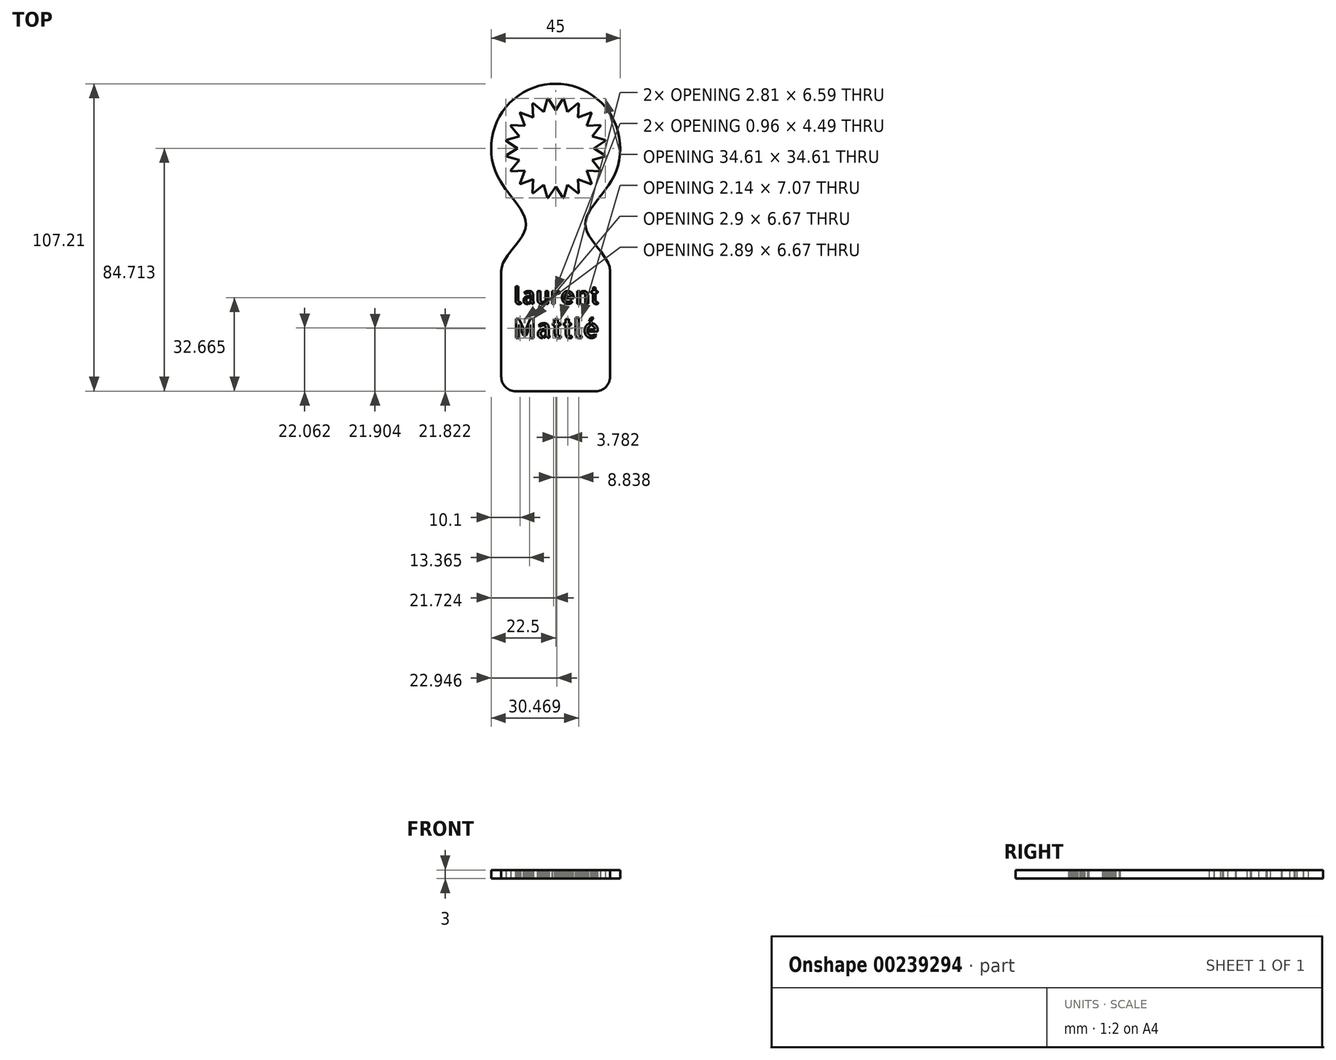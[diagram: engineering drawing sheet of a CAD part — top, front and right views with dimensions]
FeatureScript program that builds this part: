
annotation { "Feature Type Name" : "Feature", "Feature Type Description" : "" }
export const myFeature = defineFeature(function(context is Context, id is Id, definition is map)
    precondition{}
    {
        {
            var Q0;
            Q0=qCreatedBy(makeId("Top.planeOp"),FACE);
            var sketch = newSketch(context, id + "F0", { "sketchPlane" : qUnion([Q0])});
            skCircle(sketch, "E0", {"center": v(0, 8.25) * mm, "radius": 22.5 * mm});
            skLineSegment(sketch, "E1.bottom", {"start": v(-18.96, -34.53) * mm, "end": v(18.96, -34.53) * mm});
            skLineSegment(sketch, "E1.top", {"start": v(-13.96, -76.46) * mm, "end": v(13.96, -76.46) * mm});
            skLineSegment(sketch, "E1.left", {"start": v(-18.96, -34.53) * mm, "end": v(-18.96, -71.46) * mm});
            skLineSegment(sketch, "E1.right", {"start": v(18.96, -34.53) * mm, "end": v(18.96, -71.46) * mm});
            skFitSpline(sketch, "E2", {"points": [v(-19.33, -3.26) * mm, v(-10.41, -19.12) * mm, v(-18.96, -34.53) * mm], "startDerivative": vector(18.85, -32.07) * mm, "endDerivative": vector(0, -31.43) * mm});
            skFitSpline(sketch, "E3.MirrorCS", {"points": [v(19.33, -3.26) * mm, v(10.41, -19.12) * mm, v(18.96, -34.53) * mm], "startDerivative": vector(-18.85, -32.07) * mm, "endDerivative": vector(0, -31.43) * mm});
            skPoint(sketch, "E4.visualSharp", {"position": v(-18.96, -76.46) * mm});
            skArc(sketch, "E4.filletArc", {"start": v(-18.96, -71.46) * mm, "mid": v(-17.5, -75) * mm, "end": v(-13.96, -76.46) * mm});
            skPoint(sketch, "E5.visualSharp", {"position": v(18.96, -76.46) * mm});
            skArc(sketch, "E5.filletArc", {"start": v(13.96, -76.46) * mm, "mid": v(17.5, -75) * mm, "end": v(18.96, -71.46) * mm});
            skCircle(sketch, "E6", {"center": v(0, 8.25) * mm, "radius": 17.5 * mm});
            skLineSegment(sketch, "E7", {"start": v(-2.6, 25.56) * mm, "end": v(0, 21.59) * mm});
            skLineSegment(sketch, "E8", {"start": v(0, 21.59) * mm, "end": v(2.6, 25.56) * mm});
            skLineSegment(sketch, "E9.1.0", {"start": v(-7.82, 23.9) * mm, "end": v(-4.12, 20.93) * mm});
            skLineSegment(sketch, "E9.1.1", {"start": v(-4.12, 20.93) * mm, "end": v(-2.88, 25.51) * mm});
            skLineSegment(sketch, "E9.2.0", {"start": v(-12.27, 20.73) * mm, "end": v(-7.84, 19.04) * mm});
            skLineSegment(sketch, "E9.2.1", {"start": v(-7.84, 19.04) * mm, "end": v(-8.07, 23.78) * mm});
            skLineSegment(sketch, "E10.2.3.0", {"start": v(-15.53, 16.32) * mm, "end": v(-10.79, 16.1) * mm});
            skLineSegment(sketch, "E10.3.3.0", {"start": v(-10.79, 16.1) * mm, "end": v(-12.47, 20.53) * mm});
            skLineSegment(sketch, "E10.2.4.0", {"start": v(-17.26, 11.13) * mm, "end": v(-12.68, 12.37) * mm});
            skLineSegment(sketch, "E10.3.4.0", {"start": v(-12.68, 12.37) * mm, "end": v(-15.66, 16.07) * mm});
            skLineSegment(sketch, "E10.2.5.0", {"start": v(-17.3, 5.66) * mm, "end": v(-13.33, 8.25) * mm});
            skLineSegment(sketch, "E10.3.5.0", {"start": v(-13.33, 8.25) * mm, "end": v(-17.3, 10.85) * mm});
            skLineSegment(sketch, "E10.2.6.0", {"start": v(-15.66, 0.44) * mm, "end": v(-12.68, 4.13) * mm});
            skLineSegment(sketch, "E10.3.6.0", {"start": v(-12.68, 4.13) * mm, "end": v(-17.26, 5.38) * mm});
            skLineSegment(sketch, "E10.2.7.0", {"start": v(-12.47, -4.02) * mm, "end": v(-10.79, 0.42) * mm});
            skLineSegment(sketch, "E10.3.7.0", {"start": v(-10.79, 0.42) * mm, "end": v(-15.53, 0.18) * mm});
            skLineSegment(sketch, "E10.2.8.0", {"start": v(-8.07, -7.27) * mm, "end": v(-7.84, -2.53) * mm});
            skLineSegment(sketch, "E10.3.8.0", {"start": v(-7.84, -2.53) * mm, "end": v(-12.27, -4.22) * mm});
            skLineSegment(sketch, "E10.2.9.0", {"start": v(-2.88, -9) * mm, "end": v(-4.12, -4.43) * mm});
            skLineSegment(sketch, "E10.3.9.0", {"start": v(-4.12, -4.43) * mm, "end": v(-7.82, -7.4) * mm});
            skLineSegment(sketch, "E10.2.10.0", {"start": v(2.6, -9.05) * mm, "end": v(0, -5.08) * mm});
            skLineSegment(sketch, "E10.3.10.0", {"start": v(0, -5.08) * mm, "end": v(-2.6, -9.05) * mm});
            skLineSegment(sketch, "E10.2.11.0", {"start": v(7.82, -7.4) * mm, "end": v(4.12, -4.43) * mm});
            skLineSegment(sketch, "E10.3.11.0", {"start": v(4.12, -4.43) * mm, "end": v(2.88, -9) * mm});
            skLineSegment(sketch, "E10.2.12.0", {"start": v(12.27, -4.22) * mm, "end": v(7.84, -2.53) * mm});
            skLineSegment(sketch, "E10.3.12.0", {"start": v(7.84, -2.53) * mm, "end": v(8.07, -7.27) * mm});
            skLineSegment(sketch, "E10.2.13.0", {"start": v(15.53, 0.18) * mm, "end": v(10.79, 0.42) * mm});
            skLineSegment(sketch, "E10.3.13.0", {"start": v(10.79, 0.42) * mm, "end": v(12.47, -4.02) * mm});
            skLineSegment(sketch, "E10.2.14.0", {"start": v(17.26, 5.38) * mm, "end": v(12.68, 4.13) * mm});
            skLineSegment(sketch, "E10.3.14.0", {"start": v(12.68, 4.13) * mm, "end": v(15.66, 0.44) * mm});
            skLineSegment(sketch, "E10.2.15.0", {"start": v(17.3, 10.85) * mm, "end": v(13.33, 8.25) * mm});
            skLineSegment(sketch, "E10.3.15.0", {"start": v(13.33, 8.25) * mm, "end": v(17.3, 5.66) * mm});
            skLineSegment(sketch, "E10.2.16.0", {"start": v(15.66, 16.07) * mm, "end": v(12.68, 12.37) * mm});
            skLineSegment(sketch, "E10.3.16.0", {"start": v(12.68, 12.37) * mm, "end": v(17.26, 11.13) * mm});
            skLineSegment(sketch, "E10.2.17.0", {"start": v(12.47, 20.53) * mm, "end": v(10.79, 16.1) * mm});
            skLineSegment(sketch, "E10.3.17.0", {"start": v(10.79, 16.1) * mm, "end": v(15.53, 16.32) * mm});
            skLineSegment(sketch, "E10.2.18.0", {"start": v(8.07, 23.78) * mm, "end": v(7.84, 19.04) * mm});
            skLineSegment(sketch, "E10.3.18.0", {"start": v(7.84, 19.04) * mm, "end": v(12.27, 20.73) * mm});
            skLineSegment(sketch, "E10.2.19.0", {"start": v(2.88, 25.51) * mm, "end": v(4.12, 20.93) * mm});
            skLineSegment(sketch, "E10.3.19.0", {"start": v(4.12, 20.93) * mm, "end": v(7.82, 23.9) * mm});
            skSolve(sketch);
        }
        {
            var Q0;
            {var subQ27=sQuery(id+"F0.wireOp",EDGE,"E0");var subQ28=makeQuery(id+"F0.imprint","INTERSECT",VERTEX,{"derivedFrom":[subQ27,sQuery(id+"F0.wireOp",EDGE,"E2")]});Q0=makeQuery(id+"F0.imprint","IMPRINT",FACE,{"disambiguationData":[TD([[makeQuery(id+"F0.imprint","IMPRINT",EDGE,{"disambiguationData":[TD([[subQ28,-1.0]])],"derivedFrom":subQ27}),1.0]])]});}
            var Q1;
            {var subQ0=sQuery(id+"F0.wireOp",EDGE,"E10.2.4.0");Q1=makeQuery(id+"F0.imprint","IMPRINT",FACE,{"disambiguationData":[TD([[makeQuery(id+"F0.imprint","IMPRINT",EDGE,{"derivedFrom":subQ0}),1.0]])]});}
            var Q2;
            {var subQ0=sQuery(id+"F0.wireOp",EDGE,"E10.2.3.0");Q2=makeQuery(id+"F0.imprint","IMPRINT",FACE,{"disambiguationData":[TD([[makeQuery(id+"F0.imprint","IMPRINT",EDGE,{"derivedFrom":subQ0}),1.0]])]});}
            var Q3;
            {var subQ0=sQuery(id+"F0.wireOp",EDGE,"E10.2.5.0");Q3=makeQuery(id+"F0.imprint","IMPRINT",FACE,{"disambiguationData":[TD([[makeQuery(id+"F0.imprint","IMPRINT",EDGE,{"derivedFrom":subQ0}),1.0]])]});}
            var Q4;
            {var subQ0=sQuery(id+"F0.wireOp",EDGE,"E10.2.6.0");Q4=makeQuery(id+"F0.imprint","IMPRINT",FACE,{"disambiguationData":[TD([[makeQuery(id+"F0.imprint","IMPRINT",EDGE,{"derivedFrom":subQ0}),1.0]])]});}
            var Q5;
            {var subQ0=sQuery(id+"F0.wireOp",EDGE,"E10.2.7.0");Q5=makeQuery(id+"F0.imprint","IMPRINT",FACE,{"disambiguationData":[TD([[makeQuery(id+"F0.imprint","IMPRINT",EDGE,{"derivedFrom":subQ0}),1.0]])]});}
            var Q6;
            {var subQ0=sQuery(id+"F0.wireOp",EDGE,"E10.2.8.0");Q6=makeQuery(id+"F0.imprint","IMPRINT",FACE,{"disambiguationData":[TD([[makeQuery(id+"F0.imprint","IMPRINT",EDGE,{"derivedFrom":subQ0}),1.0]])]});}
            var Q7;
            {var subQ0=sQuery(id+"F0.wireOp",EDGE,"E10.2.9.0");Q7=makeQuery(id+"F0.imprint","IMPRINT",FACE,{"disambiguationData":[TD([[makeQuery(id+"F0.imprint","IMPRINT",EDGE,{"derivedFrom":subQ0}),1.0]])]});}
            var Q8;
            {var subQ0=sQuery(id+"F0.wireOp",EDGE,"E10.2.10.0");Q8=makeQuery(id+"F0.imprint","IMPRINT",FACE,{"disambiguationData":[TD([[makeQuery(id+"F0.imprint","IMPRINT",EDGE,{"derivedFrom":subQ0}),1.0]])]});}
            var Q9;
            {var subQ0=sQuery(id+"F0.wireOp",EDGE,"E10.2.11.0");Q9=makeQuery(id+"F0.imprint","IMPRINT",FACE,{"disambiguationData":[TD([[makeQuery(id+"F0.imprint","IMPRINT",EDGE,{"derivedFrom":subQ0}),1.0]])]});}
            var Q10;
            {var subQ0=sQuery(id+"F0.wireOp",EDGE,"E10.2.12.0");Q10=makeQuery(id+"F0.imprint","IMPRINT",FACE,{"disambiguationData":[TD([[makeQuery(id+"F0.imprint","IMPRINT",EDGE,{"derivedFrom":subQ0}),1.0]])]});}
            var Q11;
            {var subQ0=sQuery(id+"F0.wireOp",EDGE,"E10.2.13.0");Q11=makeQuery(id+"F0.imprint","IMPRINT",FACE,{"disambiguationData":[TD([[makeQuery(id+"F0.imprint","IMPRINT",EDGE,{"derivedFrom":subQ0}),1.0]])]});}
            var Q12;
            {var subQ0=sQuery(id+"F0.wireOp",EDGE,"E10.2.14.0");Q12=makeQuery(id+"F0.imprint","IMPRINT",FACE,{"disambiguationData":[TD([[makeQuery(id+"F0.imprint","IMPRINT",EDGE,{"derivedFrom":subQ0}),1.0]])]});}
            var Q13;
            {var subQ0=sQuery(id+"F0.wireOp",EDGE,"E10.2.15.0");Q13=makeQuery(id+"F0.imprint","IMPRINT",FACE,{"disambiguationData":[TD([[makeQuery(id+"F0.imprint","IMPRINT",EDGE,{"derivedFrom":subQ0}),1.0]])]});}
            var Q14;
            {var subQ0=sQuery(id+"F0.wireOp",EDGE,"E10.2.16.0");Q14=makeQuery(id+"F0.imprint","IMPRINT",FACE,{"disambiguationData":[TD([[makeQuery(id+"F0.imprint","IMPRINT",EDGE,{"derivedFrom":subQ0}),1.0]])]});}
            var Q15;
            {var subQ0=sQuery(id+"F0.wireOp",EDGE,"E10.2.17.0");Q15=makeQuery(id+"F0.imprint","IMPRINT",FACE,{"disambiguationData":[TD([[makeQuery(id+"F0.imprint","IMPRINT",EDGE,{"derivedFrom":subQ0}),1.0]])]});}
            var Q16;
            {var subQ0=sQuery(id+"F0.wireOp",EDGE,"E10.2.18.0");Q16=makeQuery(id+"F0.imprint","IMPRINT",FACE,{"disambiguationData":[TD([[makeQuery(id+"F0.imprint","IMPRINT",EDGE,{"derivedFrom":subQ0}),1.0]])]});}
            var Q17;
            {var subQ0=sQuery(id+"F0.wireOp",EDGE,"E10.2.19.0");Q17=makeQuery(id+"F0.imprint","IMPRINT",FACE,{"disambiguationData":[TD([[makeQuery(id+"F0.imprint","IMPRINT",EDGE,{"derivedFrom":subQ0}),1.0]])]});}
            var Q18;
            {var subQ0=sQuery(id+"F0.wireOp",EDGE,"E7");Q18=makeQuery(id+"F0.imprint","IMPRINT",FACE,{"disambiguationData":[TD([[makeQuery(id+"F0.imprint","IMPRINT",EDGE,{"derivedFrom":subQ0}),1.0]])]});}
            var Q19;
            {var subQ0=sQuery(id+"F0.wireOp",EDGE,"E9.1.0");Q19=makeQuery(id+"F0.imprint","IMPRINT",FACE,{"disambiguationData":[TD([[makeQuery(id+"F0.imprint","IMPRINT",EDGE,{"derivedFrom":subQ0}),1.0]])]});}
            var Q20;
            {var subQ0=sQuery(id+"F0.wireOp",EDGE,"E9.2.0");Q20=makeQuery(id+"F0.imprint","IMPRINT",FACE,{"disambiguationData":[TD([[makeQuery(id+"F0.imprint","IMPRINT",EDGE,{"derivedFrom":subQ0}),1.0]])]});}
            var Q21;
            Q21=makeQuery(id+"F0.imprint","IMPRINT",FACE,{"disambiguationData":[TD([[makeQuery(id+"F0.imprint","IMPRINT",EDGE,{"derivedFrom":sQuery(id+"F0.wireOp",EDGE,"E1.bottom")}),1.0]])]});
            var Q22;
            Q22=makeQuery(id+"F0.imprint","IMPRINT",FACE,{"disambiguationData":[TD([[makeQuery(id+"F0.imprint","IMPRINT",EDGE,{"derivedFrom":sQuery(id+"F0.wireOp",EDGE,"E1.bottom")}),-1.0]])]});
            extrude(context, id + "F1", {"entities" : qUnion([Q0, Q1, Q2, Q3, Q4, Q5, Q6, Q7, Q8, Q9, Q10, Q11, Q12, Q13, Q14, Q15, Q16, Q17, Q18, Q19, Q20, Q21, Q22]), "depth" : 3 * mm});
        }
        {
            var Q0;
            Q0=makeQuery(id+"F1.opExtrude","CAP_FACE",FACE,{"disambiguationData":[OSD([sQuery(id+"F0.wireOp",EDGE,"E0"),sQuery(id+"F0.wireOp",EDGE,"E1.top"),sQuery(id+"F0.wireOp",EDGE,"E1.left"),sQuery(id+"F0.wireOp",EDGE,"E1.right"),sQuery(id+"F0.wireOp",EDGE,"E2"),sQuery(id+"F0.wireOp",EDGE,"E3.MirrorCS"),sQuery(id+"F0.wireOp",EDGE,"E4.filletArc"),sQuery(id+"F0.wireOp",EDGE,"E5.filletArc"),sQuery(id+"F0.wireOp",EDGE,"E6"),sQuery(id+"F0.wireOp",EDGE,"E7"),sQuery(id+"F0.wireOp",EDGE,"E8"),sQuery(id+"F0.wireOp",EDGE,"E9.1.0"),sQuery(id+"F0.wireOp",EDGE,"E9.1.1"),sQuery(id+"F0.wireOp",EDGE,"E9.2.0"),sQuery(id+"F0.wireOp",EDGE,"E9.2.1"),sQuery(id+"F0.wireOp",EDGE,"E10.2.3.0"),sQuery(id+"F0.wireOp",EDGE,"E10.3.3.0"),sQuery(id+"F0.wireOp",EDGE,"E10.2.4.0"),sQuery(id+"F0.wireOp",EDGE,"E10.3.4.0"),sQuery(id+"F0.wireOp",EDGE,"E10.2.5.0"),sQuery(id+"F0.wireOp",EDGE,"E10.3.5.0"),sQuery(id+"F0.wireOp",EDGE,"E10.2.6.0"),sQuery(id+"F0.wireOp",EDGE,"E10.3.6.0"),sQuery(id+"F0.wireOp",EDGE,"E10.2.7.0"),sQuery(id+"F0.wireOp",EDGE,"E10.3.7.0"),sQuery(id+"F0.wireOp",EDGE,"E10.2.8.0"),sQuery(id+"F0.wireOp",EDGE,"E10.3.8.0"),sQuery(id+"F0.wireOp",EDGE,"E10.2.9.0"),sQuery(id+"F0.wireOp",EDGE,"E10.3.9.0"),sQuery(id+"F0.wireOp",EDGE,"E10.2.10.0"),sQuery(id+"F0.wireOp",EDGE,"E10.3.10.0"),sQuery(id+"F0.wireOp",EDGE,"E10.2.11.0"),sQuery(id+"F0.wireOp",EDGE,"E10.3.11.0"),sQuery(id+"F0.wireOp",EDGE,"E10.2.12.0"),sQuery(id+"F0.wireOp",EDGE,"E10.3.12.0"),sQuery(id+"F0.wireOp",EDGE,"E10.2.13.0"),sQuery(id+"F0.wireOp",EDGE,"E10.3.13.0"),sQuery(id+"F0.wireOp",EDGE,"E10.2.14.0"),sQuery(id+"F0.wireOp",EDGE,"E10.3.14.0"),sQuery(id+"F0.wireOp",EDGE,"E10.2.15.0"),sQuery(id+"F0.wireOp",EDGE,"E10.3.15.0"),sQuery(id+"F0.wireOp",EDGE,"E10.2.16.0"),sQuery(id+"F0.wireOp",EDGE,"E10.3.16.0"),sQuery(id+"F0.wireOp",EDGE,"E10.2.17.0"),sQuery(id+"F0.wireOp",EDGE,"E10.3.17.0"),sQuery(id+"F0.wireOp",EDGE,"E10.2.18.0"),sQuery(id+"F0.wireOp",EDGE,"E10.3.18.0"),sQuery(id+"F0.wireOp",EDGE,"E10.2.19.0"),sQuery(id+"F0.wireOp",EDGE,"E10.3.19.0")])],"isStart":false});
            var sketch = newSketch(context, id + "F2", { "sketchPlane" : qUnion([Q0])});
            skText(sketch, "E11", { "text": "laurent", "fontName": "AllertaStencil-Regular.ttf"});
            skText(sketch, "E12", { "text": "Mattlé", "fontName": "AllertaStencil-Regular.ttf"});
            const initialGuessF2  = {"E11": [-0.01465, -0.04604, 1, 0, 0.00587], "E12": [-0.01468, -0.05789, 1, 0, 0.00667]};
            skSetInitialGuess(sketch, initialGuessF2);
            skSolve(sketch);
        }
        {
            var Q0;
            Q0 = qSketchRegion(id + "F2", true);
            extrude(context, id + "F3", {"entities" : qUnion([Q0]), "operationType" : NewBodyOperationType.REMOVE, "endBound" : BoundingType.THROUGH_ALL, "oppositeDirection" : true, "depth" : 25 * mm});
        }
    });
